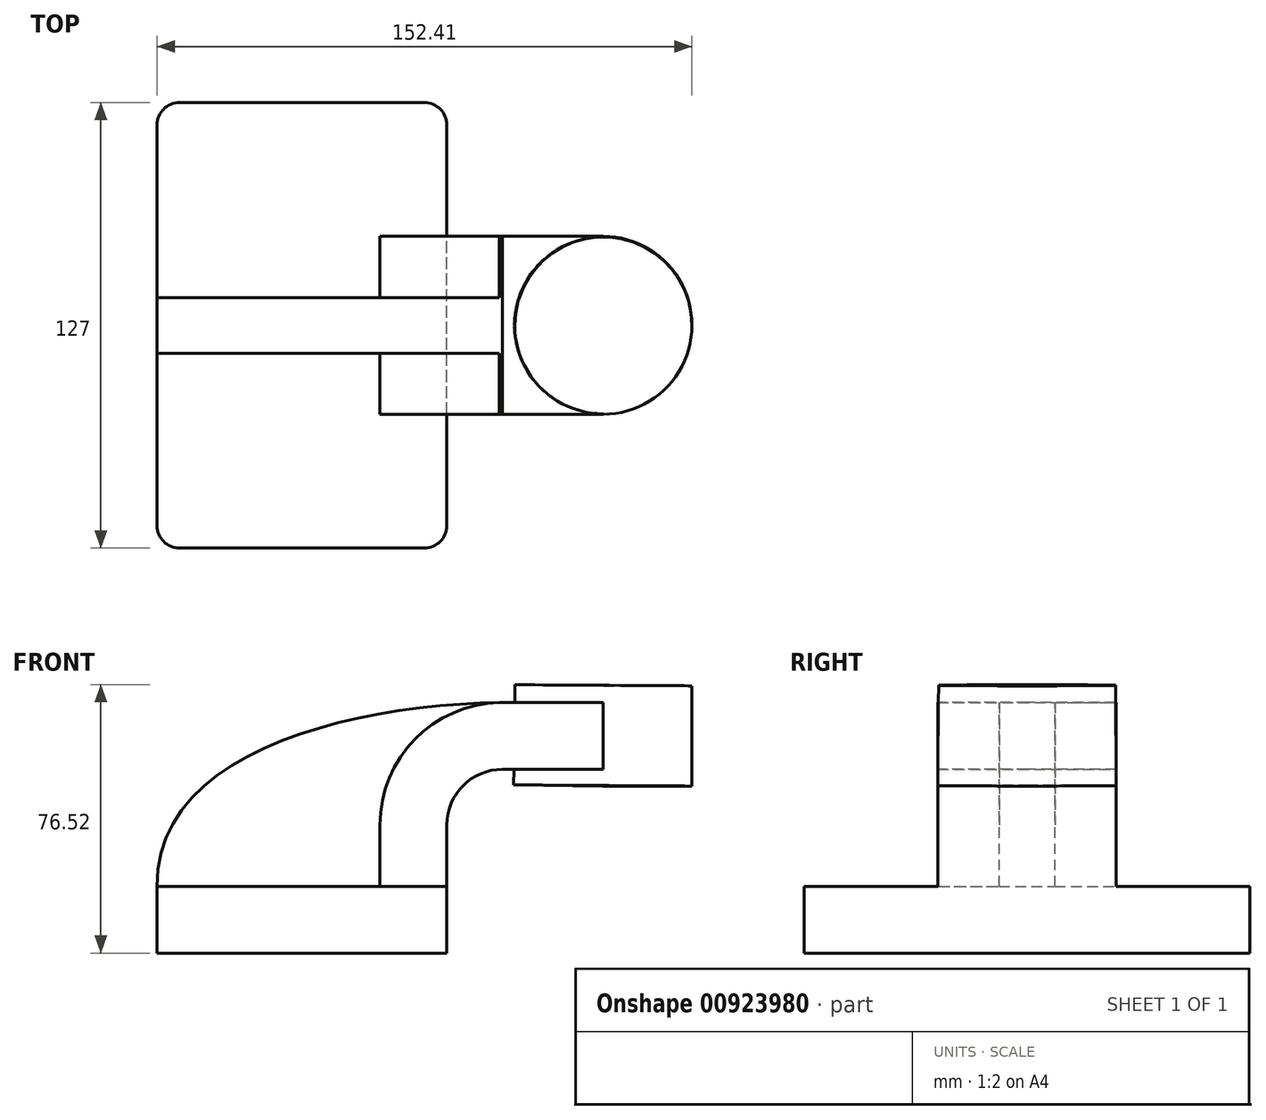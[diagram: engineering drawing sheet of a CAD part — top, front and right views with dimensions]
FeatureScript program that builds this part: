
annotation { "Feature Type Name" : "Feature", "Feature Type Description" : "" }
export const myFeature = defineFeature(function(context is Context, id is Id, definition is map)
    precondition{}
    {
        {
            var Q0;
            Q0=qCreatedBy(makeId("Front.planeOp"),FACE);
            var sketch = newSketch(context, id + "F0", { "sketchPlane" : qUnion([Q0])});
            skLineSegment(sketch, "E0.bottom", {"start": v(-41.28, 9.53) * mm, "end": v(41.28, 9.53) * mm});
            skLineSegment(sketch, "E0.top", {"start": v(-41.28, -9.53) * mm, "end": v(41.28, -9.53) * mm});
            skLineSegment(sketch, "E0.left", {"start": v(-41.28, 9.53) * mm, "end": v(-41.28, -9.52) * mm});
            skLineSegment(sketch, "E0.right", {"start": v(41.28, 9.53) * mm, "end": v(41.28, -9.53) * mm});
            skPoint(sketch, "E0.middle", {"position": v(0, 0) * mm});
            skLineSegment(sketch, "E1.bottom", {"start": v(60.32, 66.68) * mm, "end": v(111.13, 66.68) * mm});
            skLineSegment(sketch, "E1.top", {"start": v(60.32, 38.1) * mm, "end": v(111.12, 38.1) * mm});
            skLineSegment(sketch, "E1.left", {"start": v(60.32, 66.68) * mm, "end": v(60.32, 38.1) * mm});
            skLineSegment(sketch, "E1.right", {"start": v(111.13, 66.68) * mm, "end": v(111.13, 38.1) * mm});
            skPoint(sketch, "E1.middle", {"position": v(85.72, 52.39) * mm});
            skLineSegment(sketch, "E2", {"start": v(41.28, 9.53) * mm, "end": v(41.28, 27) * mm});
            skArc(sketch, "E3", {"start": v(41.28, 27) * mm, "mid": v(45.92, 38.23) * mm, "end": v(57.15, 42.88) * mm});
            skLineSegment(sketch, "E4", {"start": v(57.15, 42.88) * mm, "end": v(85.9, 42.88) * mm});
            skLineSegment(sketch, "E5.0", {"start": v(57.15, 61.93) * mm, "end": v(85.9, 61.93) * mm});
            skArc(sketch, "E5.1", {"start": v(22.23, 27) * mm, "mid": v(32.45, 51.7) * mm, "end": v(57.15, 61.93) * mm});
            skLineSegment(sketch, "E5.2", {"start": v(22.23, 9.53) * mm, "end": v(22.23, 27) * mm});
            skLineSegment(sketch, "E6", {"start": v(85.72, 38.1) * mm, "end": v(85.9, 66.68) * mm});
            skFitSpline(sketch, "E7", {"points": [v(-41.28, 9.53) * mm, v(57.15, 61.93) * mm], "startDerivative": vector(-1.69, 116.21) * mm, "endDerivative": vector(125.8, 1.3) * mm});
            skSolve(sketch);
        }
        {
            var Q0;
            Q0=makeQuery(id+"F0.imprint","IMPRINT",FACE,{"disambiguationData":[TD([[makeQuery(id+"F0.imprint","IMPRINT",EDGE,{"derivedFrom":sQuery(id+"F0.wireOp",EDGE,"E0.top")}),1.0]])]});
            extrude(context, id + "F1", {"entities" : qUnion([Q0]), "endBound" : BoundingType.SYMMETRIC, "depth" : 127 * mm, "offsetDistance" : 25.4 * mm});
        }
        {
            var Q0;
            {var subQ1=sQuery(id+"F0.wireOp",EDGE,"E2");Q0=makeQuery(id+"F0.imprint","IMPRINT",FACE,{"disambiguationData":[TD([[makeQuery(id+"F0.imprint","IMPRINT",EDGE,{"derivedFrom":subQ1}),1.0]])]});}
            var Q1;
            {var subQ0=sQuery(id+"F0.wireOp",EDGE,"E5.0");var subQ1=sQuery(id+"F0.wireOp",EDGE,"E1.left");var subQ2=makeQuery(id+"F0.imprint","INTERSECT",VERTEX,{"derivedFrom":[subQ1,subQ0]});Q1=makeQuery(id+"F0.imprint","IMPRINT",FACE,{"disambiguationData":[TD([[makeQuery(id+"F0.imprint","IMPRINT",EDGE,{"disambiguationData":[TD([[subQ2,-1.0]])],"derivedFrom":subQ1}),1.0]])]});}
            extrude(context, id + "F2", {"entities" : qUnion([Q0, Q1]), "operationType" : NewBodyOperationType.ADD, "endBound" : BoundingType.SYMMETRIC, "depth" : 50.8 * mm, "offsetDistance" : 25.4 * mm});
        }
        {
            var Q0;
            {var subQ3=sQuery(id+"F0.wireOp",EDGE,"E5.2");Q0=makeQuery(id+"F0.imprint","IMPRINT",FACE,{"disambiguationData":[TD([[makeQuery(id+"F0.imprint","IMPRINT",EDGE,{"derivedFrom":subQ3}),1.0]])]});}
            extrude(context, id + "F3", {"entities" : qUnion([Q0]), "operationType" : NewBodyOperationType.ADD, "endBound" : BoundingType.SYMMETRIC, "depth" : 15.88 * mm, "offsetDistance" : 25.4 * mm});
        }
        {
            var Q0;
            {var subQ4=sQuery(id+"F0.wireOp",EDGE,"E1.right");Q0=makeQuery(id+"F0.imprint","IMPRINT",FACE,{"disambiguationData":[TD([[makeQuery(id+"F0.imprint","IMPRINT",EDGE,{"derivedFrom":subQ4}),-1.0]])]});}
            var Q1;
            Q1=sQuery(id+"F0.wireOp",EDGE,"E6");
            revolve(context, id + "F4", {"operationType" : NewBodyOperationType.ADD, "surfaceOperationType" : NewSurfaceOperationType.NEW, "entities" : qUnion([Q0]), "axis" : qUnion([Q1]), "revolveType" : RevolveType.FULL});
        }
        {
            var Q0;
            Q0=makeQuery(id+"F1.opExtrude","CAP_EDGE",EDGE,{"disambiguationData":[OSD([sQuery(id+"F0.wireOp",EDGE,"E0.right")])],"isStart":false});
            var Q1;
            Q1=makeQuery(id+"F1.opExtrude","CAP_EDGE",EDGE,{"disambiguationData":[OSD([sQuery(id+"F0.wireOp",EDGE,"E0.right")])],"isStart":true});
            var Q2;
            Q2=makeQuery(id+"F1.opExtrude","CAP_EDGE",EDGE,{"disambiguationData":[OSD([sQuery(id+"F0.wireOp",EDGE,"E0.left")])],"isStart":true});
            var Q3;
            Q3=makeQuery(id+"F1.opExtrude","CAP_EDGE",EDGE,{"disambiguationData":[OSD([sQuery(id+"F0.wireOp",EDGE,"E0.left")])],"isStart":false});
            fillet(context, id + "F5", {"entities" : qUnion([Q0, Q1, Q2, Q3]), "radius" : 6.35 * mm, "tangentPropagation" : true, "allowEdgeOverflow" : false});
        }
    });
